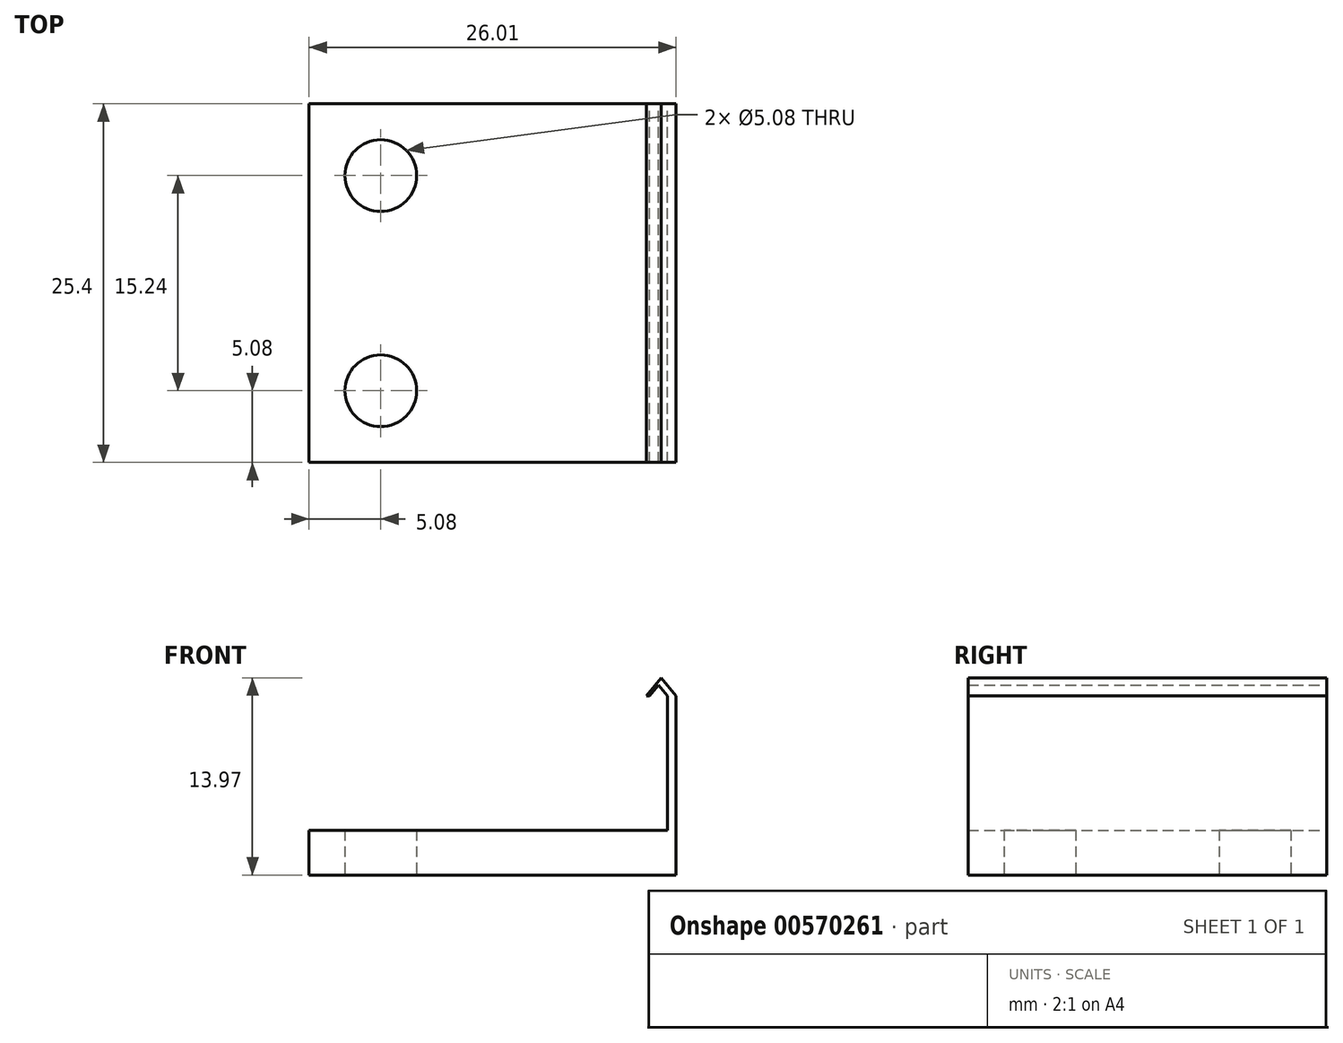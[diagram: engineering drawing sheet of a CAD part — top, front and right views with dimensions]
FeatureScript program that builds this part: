
annotation { "Feature Type Name" : "Feature", "Feature Type Description" : "" }
export const myFeature = defineFeature(function(context is Context, id is Id, definition is map)
    precondition{}
    {
        {
            var Q0;
            Q0=qCreatedBy(makeId("Front.planeOp"),FACE);
            var sketch = newSketch(context, id + "F0", { "sketchPlane" : qUnion([Q0])});
            skLineSegment(sketch, "E0.bottom", {"start": v(12.7, -1.59) * mm, "end": v(-12.7, -1.59) * mm});
            skLineSegment(sketch, "E0.top", {"start": v(12.7, 1.59) * mm, "end": v(-12.7, 1.59) * mm});
            skLineSegment(sketch, "E0.left", {"start": v(12.7, -1.59) * mm, "end": v(12.7, 1.59) * mm});
            skLineSegment(sketch, "E0.right", {"start": v(-12.7, -1.59) * mm, "end": v(-12.7, 1.59) * mm});
            skPoint(sketch, "E0.middle", {"position": v(0, 0) * mm});
            skLineSegment(sketch, "E1.bottom", {"start": v(12.7, -1.59) * mm, "end": v(13.31, -1.59) * mm});
            skLineSegment(sketch, "E1.top", {"start": v(12.7, 11.11) * mm, "end": v(13.31, 11.11) * mm});
            skLineSegment(sketch, "E1.left", {"start": v(12.7, -1.59) * mm, "end": v(12.7, 11.11) * mm});
            skLineSegment(sketch, "E1.right", {"start": v(13.31, -1.59) * mm, "end": v(13.31, 11.11) * mm});
            skLineSegment(sketch, "E2", {"start": v(11.2, 11.11) * mm, "end": v(11.44, 11.11) * mm});
            skLineSegment(sketch, "E3", {"start": v(12.07, 11.87) * mm, "end": v(12.7, 11.11) * mm});
            skLineSegment(sketch, "E4", {"start": v(11.44, 11.11) * mm, "end": v(12.07, 11.87) * mm});
            skLineSegment(sketch, "E5", {"start": v(11.2, 11.11) * mm, "end": v(12.26, 12.38) * mm});
            skLineSegment(sketch, "E6", {"start": v(12.26, 12.38) * mm, "end": v(13.31, 11.11) * mm});
            skSolve(sketch);
        }
        {
            var Q0;
            Q0 = qSketchRegion(id + "F0", true);
            extrude(context, id + "F1", {"entities" : qUnion([Q0]), "endBound" : BoundingType.SYMMETRIC, "depth" : 25.4 * mm, "offsetDistance" : 25.4 * mm});
        }
        {
            var Q0;
            Q0=makeQuery(id+"F1.opExtrude","SWEPT_FACE",FACE,{"disambiguationData":[OSD([sQuery(id+"F0.wireOp",EDGE,"E0.bottom"),sQuery(id+"F0.wireOp",EDGE,"E1.bottom")])]});
            var sketch = newSketch(context, id + "F2", { "sketchPlane" : qUnion([Q0])});
            skCircle(sketch, "E7", {"center": v(-7.62, 7.62) * mm, "radius": 2.54 * mm});
            skCircle(sketch, "E8", {"center": v(-7.62, -7.62) * mm, "radius": 2.54 * mm});
            skSolve(sketch);
        }
        {
            var Q0;
            Q0=makeQuery(id+"F2.imprint","IMPRINT",FACE,{"disambiguationData":[TD([[makeQuery(id+"F2.imprint","IMPRINT",EDGE,{"derivedFrom":sQuery(id+"F2.wireOp",EDGE,"E7")}),1.0]])]});
            var Q1;
            Q1=makeQuery(id+"F2.imprint","IMPRINT",FACE,{"disambiguationData":[TD([[makeQuery(id+"F2.imprint","IMPRINT",EDGE,{"derivedFrom":sQuery(id+"F2.wireOp",EDGE,"E8")}),1.0]])]});
            extrude(context, id + "F3", {"entities" : qUnion([Q0, Q1]), "operationType" : NewBodyOperationType.REMOVE, "endBound" : BoundingType.THROUGH_ALL, "oppositeDirection" : true, "depth" : 25.4 * mm, "offsetDistance" : 25.4 * mm});
        }
    });
